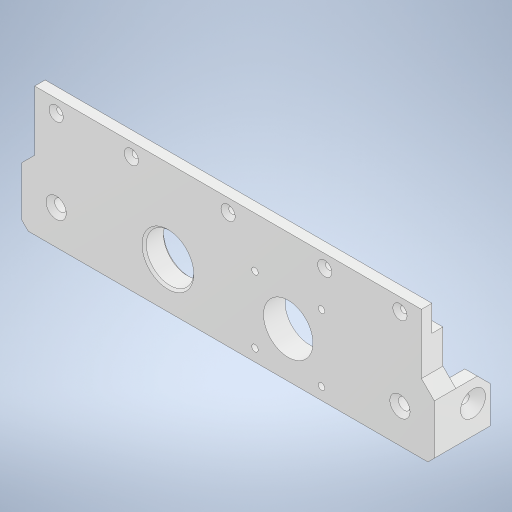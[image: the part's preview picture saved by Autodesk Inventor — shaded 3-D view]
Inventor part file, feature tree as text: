
AUTODESK INVENTOR PART (.ipt)
format: ipt  version: 2024.1 (Build 281209000, 209)  size: 490,496 bytes
history: native  units: in
note: dims shown in document units (in); Inventor stores cm internally (conversion verified against a paired STEP export)
features: extrude x18, sketch x18, chamfer x15
ambient origin geometry x8: Origin, YZ Plane, XZ Plane, XY Plane, X Axis, Y Axis, Z Axis, Center Point
bodies: Solid1 (feature_tree)
feature tree (51):
  extrude  "Extrusion1"  Depth=2.3622in
  extrude  "Extrusion4"  Depth=0.3937in
  extrude  "Extrusion5"  Depth=2.4409in
  extrude  "Extrusion6"  Depth=0.2362in
  extrude  "Extrusion7"  Depth=0.6299in
  chamfer  "Chamfer1"  Distance=0.7874in
  extrude  "Extrusion8"  Depth=0.0787in TaperAngle=45.0deg
  chamfer  "Chamfer2"  [1 undecoded]
  extrude  "Extrusion9"  Depth=0.0787in
  chamfer  "Chamfer3"  [1 undecoded]
  extrude  "Extrusion10"  Depth=0.0787in TaperAngle=45.0deg
  chamfer  "Chamfer4"  Distance=0.1181in
  extrude  "Extrusion11"  Depth=0.0787in
  chamfer  "Chamfer6"  Distance=0.1181in
  extrude  "Extrusion12"  Depth=0.0787in
  chamfer  "Chamfer7"  Distance=0.1181in
  extrude  "Extrusion13"  Depth=0.2362in
  extrude  "Extrusion14"  Depth=0.2362in
  extrude  "Extrusion15"  Depth=0.2362in
  chamfer  "Chamfer8"  Distance=0.2362in
  chamfer  "Chamfer9"  Distance=0.2362in
  extrude  "Extrusion16"  Depth=0.3937in
  chamfer  "Chamfer11"  Distance=0.3937in
  chamfer  "Chamfer12"  Distance=1.378in
  extrude  "Extrusion17"  Depth=0.0787in
  chamfer  "Chamfer13"  Distance=3.5433in
  chamfer  "Chamfer14"  [1 undecoded]
  chamfer  "Chamfer15"  Distance=0.0787in Angle=45.0deg
  extrude  "Extrusion18"  Depth=0.0787in
  chamfer  "Chamfer16"  Distance=0.3937in
  extrude  "Extrusion19"  Depth=0.0787in
  extrude  "Extrusion20"  TaperAngle=0.0deg  [1 undecoded]
  chamfer  "Chamfer18"  Distance=0.0787in Angle=45.0deg
  sketch  "Sketch1"  dims[d0=7.0866in d1=2.3622in]
  sketch  "Sketch4"  dims[d2=0.3937in d3=0.0in d16=0.9055in]
  sketch  "Sketch5"  dims[d17=0.8327in d18=2.4409in]
  sketch  "Sketch6"  dims[d19=0.0in d20=0.0in d21=0.2362in]
  sketch  "Sketch7"  dims[d22=0.6299in d23=0.0in d24=0.5551in]
  sketch  "Sketch8"  dims[d25=0.2362in]
  sketch  "Sketch9"  dims[d26=0.5551in]
  sketch  "Sketch10"  dims[d27=0.2362in d28=0.7874in d29=0.0in]
  sketch  "Sketch11"  dims[d30=0.0in d31=0.0in d32=0.1181in d33=0.0787in d34=45.0deg]
  sketch  "Sketch12"  dims[d35=0.8701in]
  sketch  "Sketch13"  dims[d36=0.8327in]
  sketch  "Sketch14"  dims[d37=2.4409in d38=0.0in d39=0.0in]
  sketch  "Sketch15"  dims[d40=0.0394in d41=0.0787in d42=45.0deg d43=0.1575in]
  sketch  "Sketch16"  dims[d44=0.3937in]
  sketch  "Sketch17"  dims[d45=0.1575in]
  sketch  "Sketch18"  dims[d46=0.3937in]
  sketch  "Sketch19"  dims[d47=0.315in]
  sketch  "Sketch20"  dims[d48=0.315in d49=0.0in d50=0.0in d51=0.1378in d52=0.0787in d53=45.0deg d54=0.1181in d55=0.1181in d56=0.1181in d57=0.1181in d58=0.1181in d59=0.2362in d60=0.2362in d61=0.2362in d62=0.2362in d63=0.2362in d64=0.3937in d65=0.3937in d66=1.378in d67=1.378in d68=3.5433in d69=0.0in d70=0.0in d71=0.0709in d72=0.0787in d73=45.0deg d77=0.1575in d78=0.3937in d79=0.315in d80=0.0in d81=0.0in d82=0.1181in d83=0.0787in d84=45.0deg d85=0.1181in d86=0.1181in d87=0.1181in d88=0.1181in d89=0.6102in d90=0.6102in d91=0.6102in d93=0.6102in d94=0.6102in d95=0.6102in d96=1.2205in d97=0.6102in d98=0.0in d99=0.0in d100=0.0709in d101=0.0787in d102=45.0deg d103=0.4764in d104=0.4764in d105=0.2008in d106=0.0in d107=0.0in d108=0.0in d109=0.0in d110=0.7913in d111=1.0236in d112=0.2362in d113=0.0in d114=0.2362in d115=0.0787in d116=45.0deg d117=0.1181in d118=0.0787in d119=45.0deg d123=0.1575in d124=0.3937in d125=0.315in d126=0.0in d127=0.0in d128=0.1496in d129=0.0787in d130=45.0deg d131=0.2362in d132=0.0787in d133=45.0deg d134=1.0236in d135=1.0276in d136=0.2362in d137=0.0in d138=0.2362in d139=0.0787in d140=45.0deg d141=0.1181in d142=0.0787in d143=45.0deg d144=0.2362in d145=0.0787in d146=45.0deg d147=0.0in d148=0.0in d149=0.1378in d150=0.0787in d151=45.0deg d152=0.2126in d153=0.2126in d154=0.3937in d155=0.6299in d156=0.3937in d157=0.6299in d158=0.0in d159=0.0in d164=0.0079in d165=0.0079in d166=0.0079in d167=0.3937in d168=0.0in d169=0.0787in d170=0.0787in d171=45.0deg]
note: 4 required parameter values undecoded (feature->parameter linkage not recoverable at this tier; creation-order binding heuristic only, values carry confidence <= 0.55)
